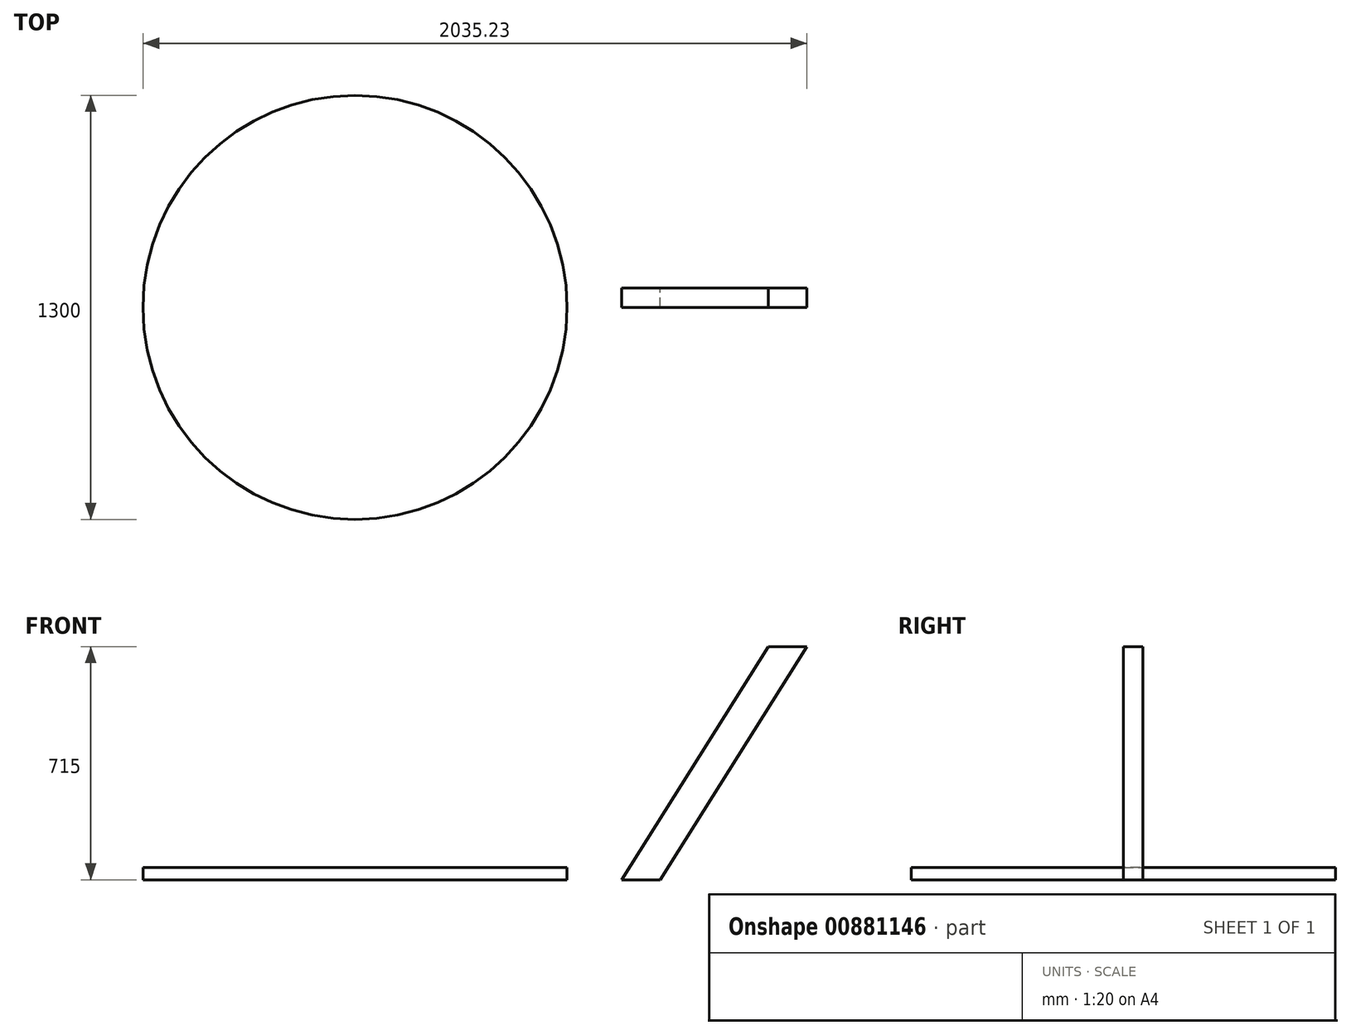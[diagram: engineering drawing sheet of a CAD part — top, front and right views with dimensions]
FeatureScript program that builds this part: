
annotation { "Feature Type Name" : "Feature", "Feature Type Description" : "" }
export const myFeature = defineFeature(function(context is Context, id is Id, definition is map)
    precondition{}
    {
        {
            var Q0;
            Q0=qCreatedBy(makeId("Front.planeOp"),FACE);
            var sketch = newSketch(context, id + "F0", { "sketchPlane" : qUnion([Q0])});
            skLineSegment(sketch, "E0", {"start": v(0, 0) * mm, "end": v(450, 715) * mm});
            skLineSegment(sketch, "E1", {"start": v(450, 715) * mm, "end": v(568.16, 715) * mm});
            skLineSegment(sketch, "E2", {"start": v(568.16, 715) * mm, "end": v(118.16, 0) * mm});
            skLineSegment(sketch, "E3", {"start": v(118.16, 0) * mm, "end": v(0, 0) * mm});
            skSolve(sketch);
        }
        {
            var Q0;
            Q0 = qSketchRegion(id + "F0", true);
            extrude(context, id + "F1", {"entities" : qUnion([Q0]), "depth" : 60 * mm, "offsetDistance" : 25 * mm});
        }
        {
            var Q0;
            Q0=qCreatedBy(makeId("Top.planeOp"),FACE);
            var sketch = newSketch(context, id + "F2", { "sketchPlane" : qUnion([Q0])});
            skCircle(sketch, "E4", {"center": v(-817.07, -59.64) * mm, "radius": 650 * mm});
            skSolve(sketch);
        }
        {
            var Q0;
            Q0=makeQuery(id+"F2.imprint","IMPRINT",FACE,{"disambiguationData":[TD([[makeQuery(id+"F2.imprint","IMPRINT",EDGE,{"derivedFrom":sQuery(id+"F2.wireOp",EDGE,"E4")}),1.0]])]});
            extrude(context, id + "F3", {"entities" : qUnion([Q0]), "depth" : 38 * mm, "offsetDistance" : 25 * mm});
        }
    });
